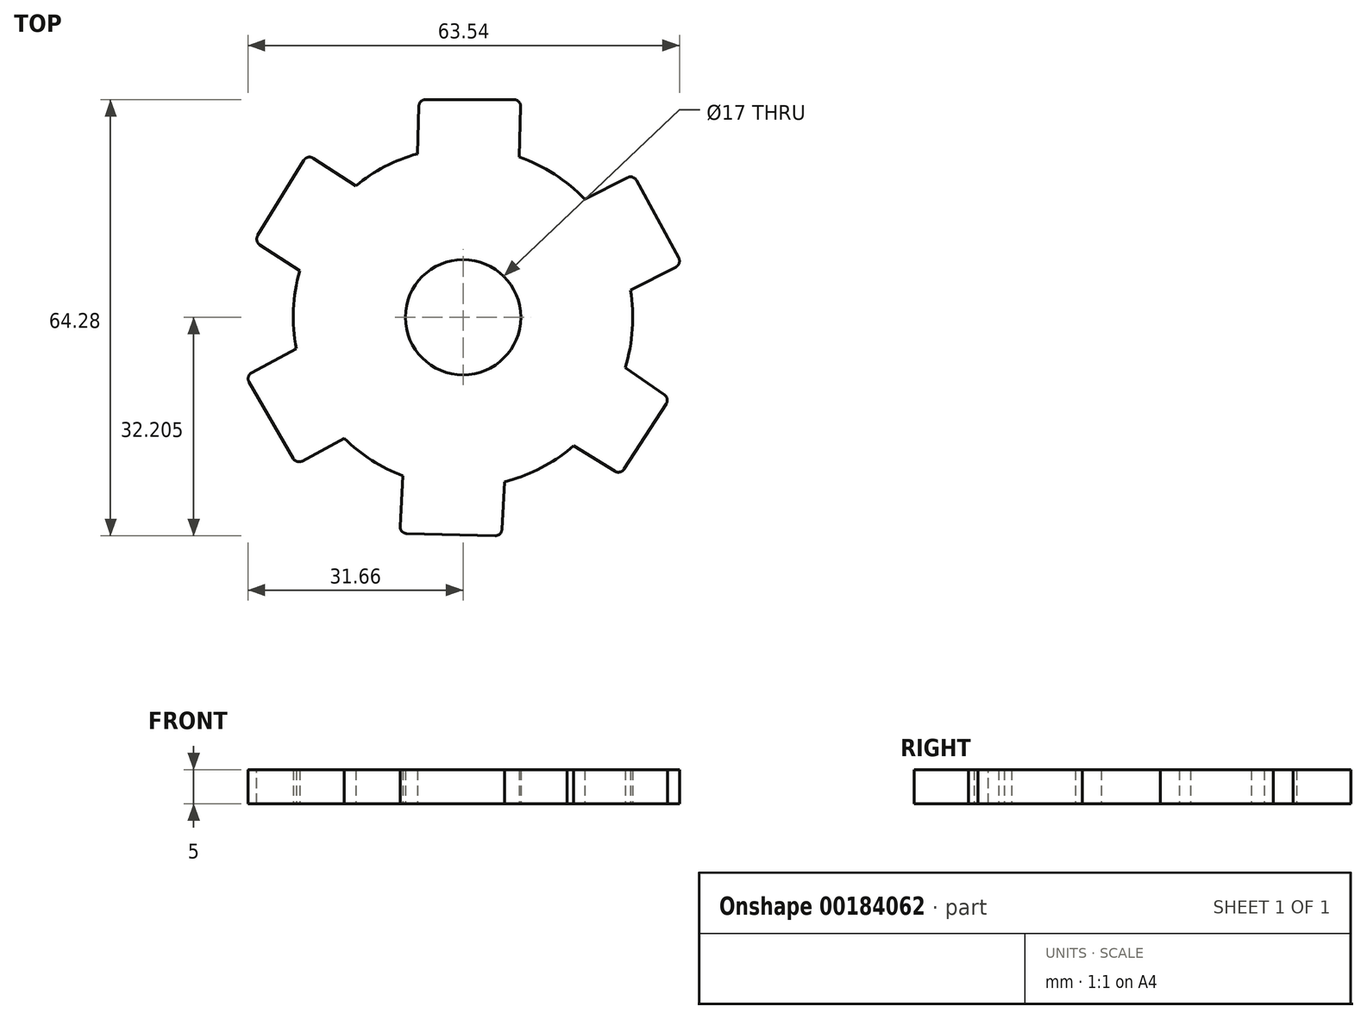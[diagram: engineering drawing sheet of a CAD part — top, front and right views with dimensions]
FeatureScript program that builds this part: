
annotation { "Feature Type Name" : "Feature", "Feature Type Description" : "" }
export const myFeature = defineFeature(function(context is Context, id is Id, definition is map)
    precondition{}
    {
        {
            var Q0;
            Q0=qCreatedBy(makeId("Top.planeOp"),FACE);
            var sketch = newSketch(context, id + "F0", { "sketchPlane" : qUnion([Q0])});
            skArc(sketch, "E0", {"start": v(-6.72, 28.1) * mm, "mid": v(-11.51, 26.2) * mm, "end": v(-15.82, 23.37) * mm});
            skLineSegment(sketch, "E1.bottom", {"start": v(-6.48, 36.1) * mm, "end": v(8.52, 36.1) * mm});
            skLineSegment(sketch, "E1.left", {"start": v(-6.48, 36.1) * mm, "end": v(-6.72, 28.1) * mm});
            skLineSegment(sketch, "E1.right", {"start": v(8.52, 36.1) * mm, "end": v(8.26, 27.6) * mm});
            skCircle(sketch, "E2", {"center": v(0, 4.02) * mm, "radius": 8.5 * mm});
            skLineSegment(sketch, "E3.1.0", {"start": v(-32.04, -4.64) * mm, "end": v(-24.57, -0.62) * mm});
            skLineSegment(sketch, "E3.1.1", {"start": v(-24.54, -17.63) * mm, "end": v(-17.5, -13.85) * mm});
            skLineSegment(sketch, "E3.1.2", {"start": v(-24.54, -17.63) * mm, "end": v(-32.04, -4.64) * mm});
            skLineSegment(sketch, "E3.2.0", {"start": v(23.52, -19.4) * mm, "end": v(16.3, -14.94) * mm});
            skLineSegment(sketch, "E4.1.0", {"start": v(25.08, 25.04) * mm, "end": v(17.94, 21.43) * mm});
            skLineSegment(sketch, "E4.1.1", {"start": v(25.08, 25.04) * mm, "end": v(32.25, 11.86) * mm});
            skLineSegment(sketch, "E4.1.2", {"start": v(32.25, 11.86) * mm, "end": v(24.67, 8.04) * mm});
            skLineSegment(sketch, "E4.2.0", {"start": v(30.45, -7.96) * mm, "end": v(23.87, -3.42) * mm});
            skLineSegment(sketch, "E4.2.1", {"start": v(30.45, -7.96) * mm, "end": v(23.19, -19.2) * mm});
            skLineSegment(sketch, "E5.1.0", {"start": v(-30.75, 15.22) * mm, "end": v(-24.05, 10.84) * mm});
            skLineSegment(sketch, "E5.1.1", {"start": v(-30.75, 15.22) * mm, "end": v(-22.92, 28.02) * mm});
            skLineSegment(sketch, "E5.1.2", {"start": v(-22.92, 28.02) * mm, "end": v(-15.82, 23.37) * mm});
            skLineSegment(sketch, "E5.2.0", {"start": v(5.67, -28.21) * mm, "end": v(6.11, -20.23) * mm});
            skLineSegment(sketch, "E5.2.1", {"start": v(5.67, -28.21) * mm, "end": v(-9.33, -27.84) * mm});
            skLineSegment(sketch, "E5.2.2", {"start": v(-9.33, -27.84) * mm, "end": v(-8.86, -19.36) * mm});
            skArc(sketch, "E6.trimOffspring", {"start": v(17.94, 21.43) * mm, "mid": v(13.46, 25.08) * mm, "end": v(8.26, 27.6) * mm});
            skArc(sketch, "E7.trimOffspring", {"start": v(23.87, -3.42) * mm, "mid": v(24.94, 2.26) * mm, "end": v(24.67, 8.04) * mm});
            skArc(sketch, "E8.trimOffspring", {"start": v(6.11, -20.23) * mm, "mid": v(10.95, -18.46) * mm, "end": v(15.33, -15.74) * mm});
            skArc(sketch, "E9.trimOffspring", {"start": v(-17.5, -13.85) * mm, "mid": v(-13.46, -17.05) * mm, "end": v(-8.86, -19.36) * mm});
            skArc(sketch, "E10.trimOffspring", {"start": v(-24.05, 10.84) * mm, "mid": v(-24.97, 5.14) * mm, "end": v(-24.57, -0.62) * mm});
            skPoint(sketch, "E11.orphan", {"position": v(31.02, -6.41) * mm});
            skPoint(sketch, "E12.orphan", {"position": v(22.3, -20.56) * mm});
            skLineSegment(sketch, "E13", {"start": v(16.3, -14.94) * mm, "end": v(15.33, -15.74) * mm});
            skSolve(sketch);
        }
        {
            var Q0;
            Q0=makeQuery(id+"F0.imprint","IMPRINT",FACE,{"disambiguationData":[TD([[makeQuery(id+"F0.imprint","IMPRINT",EDGE,{"derivedFrom":sQuery(id+"F0.wireOp",EDGE,"E0")}),1.0]])]});
            extrude(context, id + "F1", {"entities" : qUnion([Q0]), "depth" : 5 * mm});
        }
        {
            var Q0;
            Q0=makeQuery(id+"F1.opExtrude","SWEPT_EDGE",EDGE,{"disambiguationData":[OSD([sQuery(id+"F0.wireOp",EDGE,"E3.1.1"),sQuery(id+"F0.wireOp",EDGE,"E3.1.2")])]});
            var Q1;
            Q1=makeQuery(id+"F1.opExtrude","SWEPT_EDGE",EDGE,{"disambiguationData":[OSD([sQuery(id+"F0.wireOp",EDGE,"E3.1.0"),sQuery(id+"F0.wireOp",EDGE,"E3.1.2")])]});
            fillet(context, id + "F2", {"entities" : qUnion([Q0, Q1]), "radius" : 1 * mm, "tangentPropagation" : true, "allowEdgeOverflow" : false});
        }
        {
            var Q0;
            Q0=makeQuery(id+"F1.opExtrude","SWEPT_EDGE",EDGE,{"disambiguationData":[OSD([sQuery(id+"F0.wireOp",EDGE,"E5.2.1"),sQuery(id+"F0.wireOp",EDGE,"E5.2.2")])]});
            fillet(context, id + "F3", {"entities" : qUnion([Q0]), "radius" : 1 * mm, "tangentPropagation" : true, "allowEdgeOverflow" : false});
        }
        {
            var Q0;
            Q0=makeQuery(id+"F1.opExtrude","SWEPT_EDGE",EDGE,{"disambiguationData":[OSD([sQuery(id+"F0.wireOp",EDGE,"E5.1.1"),sQuery(id+"F0.wireOp",EDGE,"E5.1.2")])]});
            fillet(context, id + "F4", {"entities" : qUnion([Q0]), "radius" : 1 * mm, "tangentPropagation" : true, "allowEdgeOverflow" : false});
        }
        {
            var Q0;
            Q0=makeQuery(id+"F1.opExtrude","SWEPT_EDGE",EDGE,{"disambiguationData":[OSD([sQuery(id+"F0.wireOp",EDGE,"E5.1.0"),sQuery(id+"F0.wireOp",EDGE,"E5.1.1")])]});
            fillet(context, id + "F5", {"entities" : qUnion([Q0]), "radius" : 1 * mm, "tangentPropagation" : true, "allowEdgeOverflow" : false});
        }
        {
            var Q0;
            Q0=makeQuery(id+"F1.opExtrude","SWEPT_EDGE",EDGE,{"disambiguationData":[OSD([sQuery(id+"F0.wireOp",EDGE,"E5.2.0"),sQuery(id+"F0.wireOp",EDGE,"E5.2.1")])]});
            fillet(context, id + "F6", {"entities" : qUnion([Q0]), "radius" : 1 * mm, "tangentPropagation" : true, "allowEdgeOverflow" : false});
        }
        {
            var Q0;
            Q0=makeQuery(id+"F1.opExtrude","SWEPT_EDGE",EDGE,{"disambiguationData":[OSD([sQuery(id+"F0.wireOp",EDGE,"E3.2.0"),sQuery(id+"F0.wireOp",EDGE,"E4.2.1")])]});
            var Q1;
            Q1=makeQuery(id+"F1.opExtrude","SWEPT_EDGE",EDGE,{"disambiguationData":[OSD([sQuery(id+"F0.wireOp",EDGE,"E4.2.0"),sQuery(id+"F0.wireOp",EDGE,"E4.2.1")])]});
            var Q2;
            Q2=makeQuery(id+"F1.opExtrude","SWEPT_EDGE",EDGE,{"disambiguationData":[OSD([sQuery(id+"F0.wireOp",EDGE,"E4.1.1"),sQuery(id+"F0.wireOp",EDGE,"E4.1.2")])]});
            fillet(context, id + "F7", {"entities" : qUnion([Q0, Q1, Q2]), "radius" : 1 * mm, "tangentPropagation" : true, "allowEdgeOverflow" : false});
        }
        {
            var Q0;
            Q0=makeQuery(id+"F1.opExtrude","SWEPT_EDGE",EDGE,{"disambiguationData":[OSD([sQuery(id+"F0.wireOp",EDGE,"E4.1.0"),sQuery(id+"F0.wireOp",EDGE,"E4.1.1")])]});
            var Q1;
            Q1=makeQuery(id+"F1.opExtrude","SWEPT_EDGE",EDGE,{"disambiguationData":[OSD([sQuery(id+"F0.wireOp",EDGE,"E1.bottom"),sQuery(id+"F0.wireOp",EDGE,"E1.right")])]});
            var Q2;
            Q2=makeQuery(id+"F1.opExtrude","SWEPT_EDGE",EDGE,{"disambiguationData":[OSD([sQuery(id+"F0.wireOp",EDGE,"E1.bottom"),sQuery(id+"F0.wireOp",EDGE,"E1.left")])]});
            fillet(context, id + "F8", {"entities" : qUnion([Q0, Q1, Q2]), "radius" : 1 * mm, "tangentPropagation" : true, "allowEdgeOverflow" : false});
        }
    });
